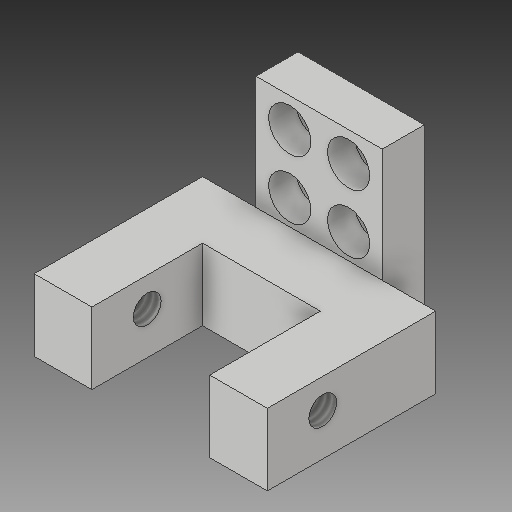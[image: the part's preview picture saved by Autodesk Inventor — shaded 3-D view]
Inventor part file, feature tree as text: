
AUTODESK INVENTOR PART (.ipt)
format: ipt  version: 2019 (Build 230136000, 136)  size: 211,456 bytes
history: native  units: mm
features: sketch x8, extrude x5, hole x3
ambient origin geometry x8: Origin, YZ Plane, XZ Plane, XY Plane, X Axis, Y Axis, Z Axis, Center Point
bodies: Solid1 (feature_tree)
feature tree (16):
  extrude  "Extrusion1"  Depth=22.0mm
  hole  "Hole1"  [1 undecoded]
  extrude  "Extrusion2"  Depth=5.0mm
  extrude  "Extrusion3"  Depth=5.0mm
  sketch  "Sketch6"  dims[d9=7.0mm d10=7.0mm]
  sketch  "Sketch7"  dims[d11=3.5mm d12=3.5mm]
  extrude  "Extrusion5"  Depth=7.0mm
  hole  "Hole4"  [1 undecoded]
  extrude  "Extrusion6"  Depth=0.5mm
  hole  "Hole5"  [1 undecoded]
  sketch  "Sketch1"  dims[d0=15.0mm d1=22.0mm]
  sketch  "Sketch2"  dims[d2=5.0mm d3=0.0mm d4=5.0mm]
  sketch  "Sketch3"  dims[d5=5.0mm d6=7.0mm]
  sketch  "Sketch4"  dims[d7=5.0mm d8=5.0mm]
  sketch  "Sketch8"  dims[d13=3.2mm d14=6.0mm d15=5.0mm d16=3.2mm d17=90.0deg d18=0.5mm d19=20.594885mm]
  sketch  "Sketch9"  dims[d20=8.5mm d21=0.0mm d22=0.0mm d23=0.0mm d24=20.0mm d25=0.0mm d26=4.0mm d27=4.0mm d28=4.0mm d29=4.0mm d30=0.0mm d31=13.15mm d32=14.0mm d33=0.5mm d34=8.5mm d35=0.0mm d42=3.0mm d43=3.5mm d44=6.575mm d45=3.0mm d46=6.575mm d47=3.5mm d62=6.35mm d63=0.0mm d64=3.302mm d65=8.331mm d66=4.0mm d67=2.0mm d68=90.0deg d69=12.3mm d70=20.594885mm d71=6.35mm d72=0.0mm d73=3.302mm d74=8.331mm d75=4.0mm d76=2.0mm d77=90.0deg d78=12.3mm d79=20.594885mm d81=13.15mm d82=7.0mm d83=13.15mm d84=7.0mm]
note: 3 required parameter values undecoded (feature->parameter linkage not recoverable at this tier; creation-order binding heuristic only, values carry confidence <= 0.55)
